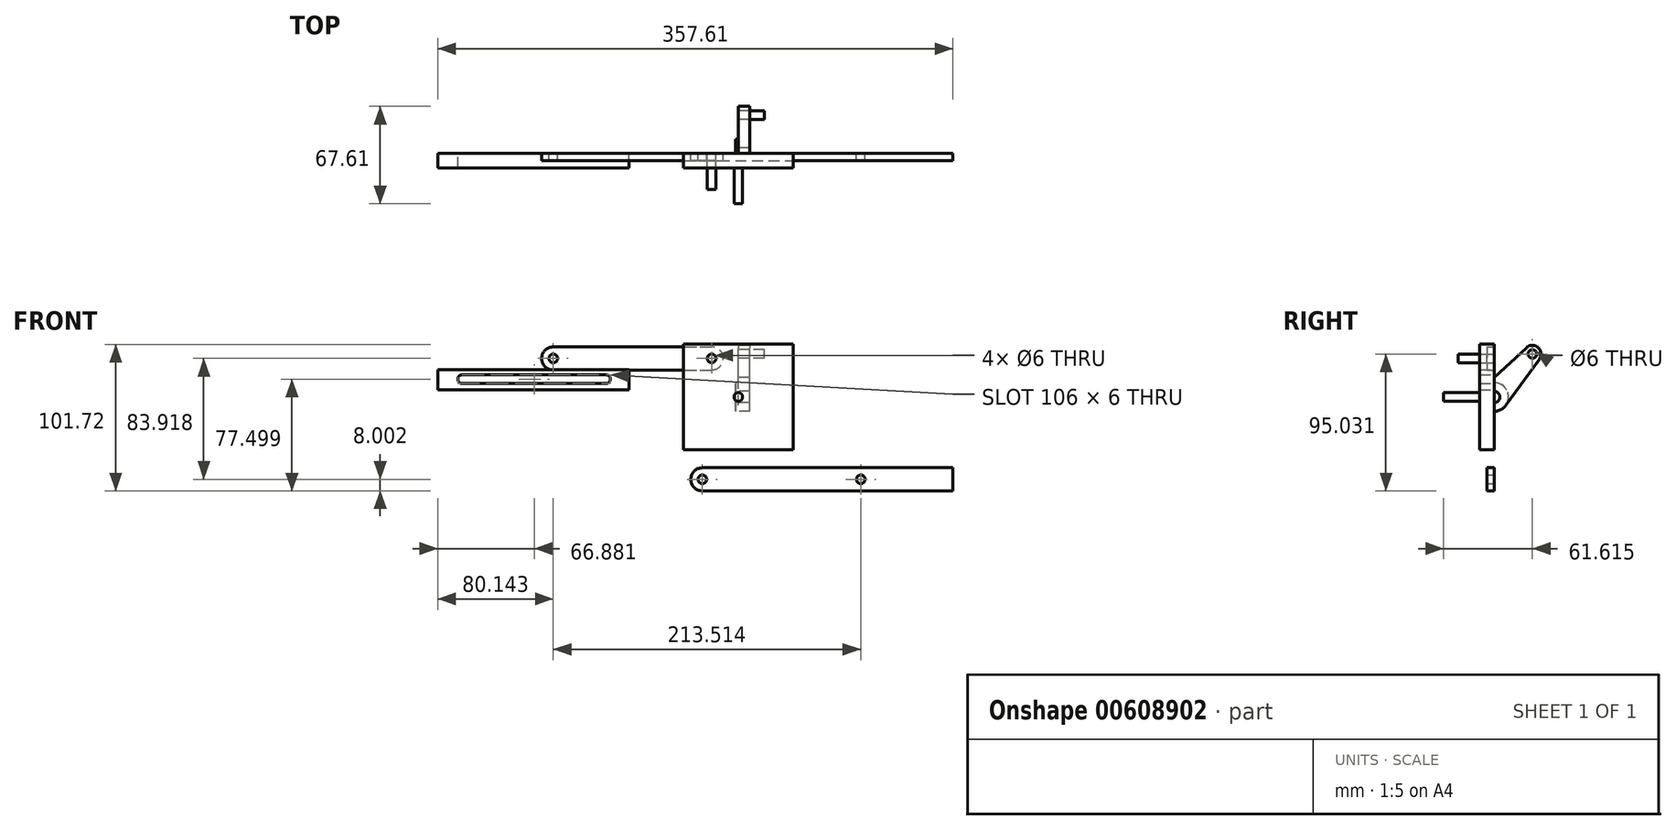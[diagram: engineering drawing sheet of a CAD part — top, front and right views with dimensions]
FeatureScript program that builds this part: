
annotation { "Feature Type Name" : "Feature", "Feature Type Description" : "" }
export const myFeature = defineFeature(function(context is Context, id is Id, definition is map)
    precondition{}
    {
        {
            var Q0;
            Q0=qCreatedBy(makeId("Front.planeOp"),FACE);
            var sketch = newSketch(context, id + "F0", { "sketchPlane" : qUnion([Q0])});
            skLineSegment(sketch, "E0.bottom", {"start": v(38.04, -36.55) * mm, "end": v(-38.04, -36.55) * mm});
            skLineSegment(sketch, "E0.top", {"start": v(38.04, 36.55) * mm, "end": v(-38.04, 36.55) * mm});
            skLineSegment(sketch, "E0.left", {"start": v(38.04, -36.55) * mm, "end": v(38.04, 36.55) * mm});
            skLineSegment(sketch, "E0.right", {"start": v(-38.04, -36.55) * mm, "end": v(-38.04, 36.55) * mm});
            skPoint(sketch, "E0.middle", {"position": v(0, 0) * mm});
            skSolve(sketch);
        }
        {
            var Q0;
            Q0=makeQuery(id+"F0.imprint","IMPRINT",FACE,{"disambiguationData":[TD([[makeQuery(id+"F0.imprint","IMPRINT",EDGE,{"derivedFrom":sQuery(id+"F0.wireOp",EDGE,"E0.bottom")}),-1.0]])]});
            extrude(context, id + "F1", {"entities" : qUnion([Q0]), "depth" : 10 * mm, "offsetDistance" : 25 * mm});
        }
        {
            var Q0;
            Q0=makeQuery(id+"F1.opExtrude","CAP_FACE",FACE,{"disambiguationData":[OSD([sQuery(id+"F0.wireOp",EDGE,"E0.bottom"),sQuery(id+"F0.wireOp",EDGE,"E0.top"),sQuery(id+"F0.wireOp",EDGE,"E0.left"),sQuery(id+"F0.wireOp",EDGE,"E0.right")])],"isStart":false});
            var sketch = newSketch(context, id + "F2", { "sketchPlane" : qUnion([Q0])});
            skCircle(sketch, "E1", {"center": v(0, 0) * mm, "radius": 3 * mm});
            skSolve(sketch);
        }
        {
            var Q0;
            Q0 = qSketchRegion(id + "F2", true);
            extrude(context, id + "F3", {"entities" : qUnion([Q0]), "operationType" : NewBodyOperationType.ADD, "depth" : 25 * mm, "offsetDistance" : 25 * mm});
        }
        {
            var Q0;
            Q0=qCreatedBy(makeId("Front.planeOp"),FACE);
            var sketch = newSketch(context, id + "F4", { "sketchPlane" : qUnion([Q0])});
            skCircle(sketch, "E2", {"center": v(-128.5, 26.75) * mm, "radius": 3 * mm});
            skArc(sketch, "E3", {"start": v(-128.5, 34.75) * mm, "mid": v(-136.5, 26.75) * mm, "end": v(-128.5, 18.75) * mm});
            skCircle(sketch, "E4", {"center": v(-18.5, 26.75) * mm, "radius": 3 * mm});
            skArc(sketch, "E5", {"start": v(-18.5, 18.75) * mm, "mid": v(-10.5, 26.75) * mm, "end": v(-18.5, 34.75) * mm});
            skLineSegment(sketch, "E6", {"start": v(-128.5, 34.75) * mm, "end": v(-18.5, 34.75) * mm});
            skLineSegment(sketch, "E7", {"start": v(-128.5, 18.75) * mm, "end": v(-18.5, 18.75) * mm});
            skSolve(sketch);
        }
        {
            var Q0;
            Q0 = qSketchRegion(id + "F4", true);
            extrude(context, id + "F5", {"entities" : qUnion([Q0]), "depth" : 5 * mm, "offsetDistance" : 25 * mm});
        }
        {
            var Q0;
            Q0=qCreatedBy(makeId("Right.planeOp"),FACE);
            var sketch = newSketch(context, id + "F6", { "sketchPlane" : qUnion([Q0])});
            skCircle(sketch, "E8", {"center": v(0, 0) * mm, "radius": 4 * mm});
            skArc(sketch, "E9", {"start": v(-6.76, 7.37) * mm, "mid": v(-6.65, -7.47) * mm, "end": v(8.1, -5.87) * mm});
            skCircle(sketch, "E10", {"center": v(26.61, 29.86) * mm, "radius": 3 * mm});
            skArc(sketch, "E11", {"start": v(31.47, 26.34) * mm, "mid": v(30.6, 34.34) * mm, "end": v(22.56, 34.28) * mm});
            skLineSegment(sketch, "E12", {"start": v(-6.76, 7.37) * mm, "end": v(22.56, 34.28) * mm});
            skLineSegment(sketch, "E13", {"start": v(8.1, -5.87) * mm, "end": v(31.47, 26.34) * mm});
            skSolve(sketch);
        }
        {
            var Q0;
            Q0 = qSketchRegion(id + "F6", true);
            extrude(context, id + "F7", {"entities" : qUnion([Q0]), "depth" : 8 * mm, "offsetDistance" : 25 * mm});
        }
        {
            var Q0;
            Q0=makeQuery(id+"F7.opExtrude","CAP_FACE",FACE,{"disambiguationData":[OSD([sQuery(id+"F6.wireOp",EDGE,"E8"),sQuery(id+"F6.wireOp",EDGE,"E9"),sQuery(id+"F6.wireOp",EDGE,"E10"),sQuery(id+"F6.wireOp",EDGE,"E11"),sQuery(id+"F6.wireOp",EDGE,"E12"),sQuery(id+"F6.wireOp",EDGE,"E13")])],"isStart":true});
            var sketch = newSketch(context, id + "F8", { "sketchPlane" : qUnion([Q0])});
            skCircle(sketch, "E14", {"center": v(0, 0) * mm, "radius": 10 * mm});
            skCircle(sketch, "E15", {"center": v(0, 0) * mm, "radius": 4 * mm});
            skSolve(sketch);
        }
        {
            var Q0;
            Q0 = qSketchRegion(id + "F8", true);
            extrude(context, id + "F9", {"entities" : qUnion([Q0]), "operationType" : NewBodyOperationType.ADD, "depth" : 2 * mm, "offsetDistance" : 25 * mm});
        }
        {
            var Q0;
            Q0=makeQuery(id+"F5.opExtrude","CAP_FACE",FACE,{"disambiguationData":[OSD([sQuery(id+"F4.wireOp",EDGE,"E2"),sQuery(id+"F4.wireOp",EDGE,"E3"),sQuery(id+"F4.wireOp",EDGE,"E4"),sQuery(id+"F4.wireOp",EDGE,"E5"),sQuery(id+"F4.wireOp",EDGE,"E6"),sQuery(id+"F4.wireOp",EDGE,"E7")])],"isStart":true});
            var sketch = newSketch(context, id + "F10", { "sketchPlane" : qUnion([Q0])});
            skCircle(sketch, "E16", {"center": v(18.5, 26.75) * mm, "radius": 3 * mm});
            skSolve(sketch);
        }
        {
            var Q0;
            Q0 = qSketchRegion(id + "F10", true);
            extrude(context, id + "F11", {"entities" : qUnion([Q0]), "oppositeDirection" : true, "depth" : 25 * mm, "offsetDistance" : 25 * mm});
        }
        {
            var Q0;
            Q0=qCreatedBy(makeId("Front.planeOp"),FACE);
            var sketch = newSketch(context, id + "F12", { "sketchPlane" : qUnion([Q0])});
            skArc(sketch, "E17", {"start": v(-191.76, 15.33) * mm, "mid": v(-194.76, 12.33) * mm, "end": v(-191.76, 9.33) * mm});
            skArc(sketch, "E18", {"start": v(-91.76, 9.33) * mm, "mid": v(-88.76, 12.33) * mm, "end": v(-91.76, 15.33) * mm});
            skLineSegment(sketch, "E19.bottom", {"start": v(-208.64, 19.06) * mm, "end": v(-75.98, 19.06) * mm});
            skLineSegment(sketch, "E19.top", {"start": v(-208.64, 5.03) * mm, "end": v(-75.98, 5.03) * mm});
            skLineSegment(sketch, "E19.left", {"start": v(-208.64, 19.06) * mm, "end": v(-208.64, 5.03) * mm});
            skLineSegment(sketch, "E19.right", {"start": v(-75.98, 19.06) * mm, "end": v(-75.98, 5.03) * mm});
            skLineSegment(sketch, "E20", {"start": v(-191.76, 15.33) * mm, "end": v(-91.76, 15.33) * mm});
            skLineSegment(sketch, "E21", {"start": v(-191.76, 9.33) * mm, "end": v(-91.76, 9.33) * mm});
            skSolve(sketch);
        }
        {
            var Q0;
            Q0 = qSketchRegion(id + "F12", true);
            extrude(context, id + "F13", {"entities" : qUnion([Q0]), "depth" : 10 * mm, "offsetDistance" : 25 * mm});
        }
        {
            var Q0;
            Q0=makeQuery(id+"F7.opExtrude","CAP_FACE",FACE,{"disambiguationData":[OSD([sQuery(id+"F6.wireOp",EDGE,"E8"),sQuery(id+"F6.wireOp",EDGE,"E9"),sQuery(id+"F6.wireOp",EDGE,"E10"),sQuery(id+"F6.wireOp",EDGE,"E11"),sQuery(id+"F6.wireOp",EDGE,"E12"),sQuery(id+"F6.wireOp",EDGE,"E13")])],"isStart":false});
            var sketch = newSketch(context, id + "F14", { "sketchPlane" : qUnion([Q0])});
            skCircle(sketch, "E22", {"center": v(26.61, 29.86) * mm, "radius": 3 * mm});
            skSolve(sketch);
        }
        {
            var Q0;
            Q0 = qSketchRegion(id + "F14", true);
            extrude(context, id + "F15", {"entities" : qUnion([Q0]), "operationType" : NewBodyOperationType.ADD, "depth" : 10 * mm, "offsetDistance" : 25 * mm});
        }
        {
            var Q0;
            Q0=makeQuery(id+"F5.opExtrude","SWEPT_BODY",BODY,{"disambiguationData":[OSD([sQuery(id+"F4.wireOp",EDGE,"E2"),sQuery(id+"F4.wireOp",EDGE,"E3"),sQuery(id+"F4.wireOp",EDGE,"E4"),sQuery(id+"F4.wireOp",EDGE,"E5"),sQuery(id+"F4.wireOp",EDGE,"E6"),sQuery(id+"F4.wireOp",EDGE,"E7")])]});
            transform(context, id + "F16", {"entities" : qUnion([Q0]), "transformType" : TransformType.TRANSLATION_3D, "dx" : 0 * mm, "dy" : -77 * mm, "dz" : 0 * mm, "makeCopy" : true});
        }
        {
            var Q0;
            Q0=makeQuery(id+"F16.opPattern","COPY",BODY,{"derivedFrom":makeQuery(id+"F5.opExtrude","SWEPT_BODY",BODY,{"disambiguationData":[OSD([sQuery(id+"F4.wireOp",EDGE,"E2"),sQuery(id+"F4.wireOp",EDGE,"E3"),sQuery(id+"F4.wireOp",EDGE,"E4"),sQuery(id+"F4.wireOp",EDGE,"E5"),sQuery(id+"F4.wireOp",EDGE,"E6"),sQuery(id+"F4.wireOp",EDGE,"E7")])]}),"instanceName":"1"});
            deleteBodies(context, id + "F17", {"entities" : qUnion([Q0])});
        }
        {
            var Q0;
            Q0=qCreatedBy(makeId("Front.planeOp"),FACE);
            var sketch = newSketch(context, id + "F18", { "sketchPlane" : qUnion([Q0])});
            skCircle(sketch, "E23", {"center": v(-24.98, -57.17) * mm, "radius": 3 * mm});
            skArc(sketch, "E24", {"start": v(-24.98, -49.17) * mm, "mid": v(-32.98, -57.17) * mm, "end": v(-24.98, -65.17) * mm});
            skCircle(sketch, "E25", {"center": v(85.02, -57.17) * mm, "radius": 3 * mm});
            skLineSegment(sketch, "E26", {"start": v(-24.98, -49.17) * mm, "end": v(148.97, -49.17) * mm});
            skLineSegment(sketch, "E27", {"start": v(-24.98, -65.17) * mm, "end": v(148.97, -65.17) * mm});
            skLineSegment(sketch, "E28", {"start": v(148.97, -49.17) * mm, "end": v(148.97, -65.17) * mm});
            skSolve(sketch);
        }
        {
            var Q0;
            Q0=makeQuery(id+"F18.imprint","IMPRINT",FACE,{"disambiguationData":[TD([[makeQuery(id+"F18.imprint","IMPRINT",EDGE,{"derivedFrom":sQuery(id+"F18.wireOp",EDGE,"E23")}),-1.0]])]});
            extrude(context, id + "F19", {"entities" : qUnion([Q0]), "depth" : 5 * mm, "offsetDistance" : 25 * mm});
        }
    });
